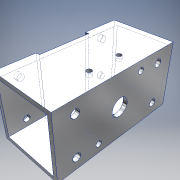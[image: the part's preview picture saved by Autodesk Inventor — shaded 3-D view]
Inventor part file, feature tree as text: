
AUTODESK INVENTOR PART (.ipt)
format: ipt  version: 2019 (Build 230136000, 136)  size: 174,080 bytes
history: native  units: in
note: dims shown in document units (in); Inventor stores cm internally (conversion verified against a paired STEP export)
features: reference x11, extrude x6, sketch x6, other x5
ambient origin geometry x8: Origin, YZ Plane, XZ Plane, XY Plane, X Axis, Y Axis, Z Axis, Center Point
bodies: Solid1 (feature_tree)
feature tree (28):
  extrude  "Extrusion1"  Depth=0.125in
  extrude  "Extrusion7"  Depth=2.0in
  sketch  "Sketch7"  dims[d12=0.125in d23=1.654in]
  sketch  "Sketch8"  dims[d24=0.125in d25=0.0in d28=0.55in]
  extrude  "Extrusion10"  Depth=1.654in
  extrude  "Extrusion11"  Depth=0.125in
  extrude  "Extrusion12"  Depth=1.0in TaperAngle=0.0deg
  extrude  "Extrusion13"  Depth=1.0in
  sketch  "Sketch1"  dims[d0=2.0in d1=0.125in]
  sketch  "Sketch6"  dims[d2=4.0in d3=0.0in d11=2.0in]
  reference  "Reference2"
  reference  "Reference3"
  reference  "Reference4"
  sketch  "Sketch9"  dims[d31=0.21in d32=1.0in d33=0.0in]
  reference  "Reference5"
  reference  "Reference6"
  reference  "Reference7"
  reference  "Reference8"
  sketch  "Sketch10"  dims[d34=1.0in d35=0.0in d36=0.19in d37=1.0in d38=0.0in d39=0.19in d40=1.0in d41=0.0in]
  reference  "Reference9"
  reference  "Reference10"
  reference  "Reference11"
  reference  "Reference12"
  parser-record x1  (decoder bookkeeping rows leaked as tree rows — omitted from the tree; the rows remain in map.json)
  other  "Drive Arm.iam"
  other  "Gearbox:1"
  other  "217-2625-026 Rev1_1"
  other  "Arm 18 inch:1"
note: 1 file-system path scrubbed to <path> (originals preserved in map.json)
